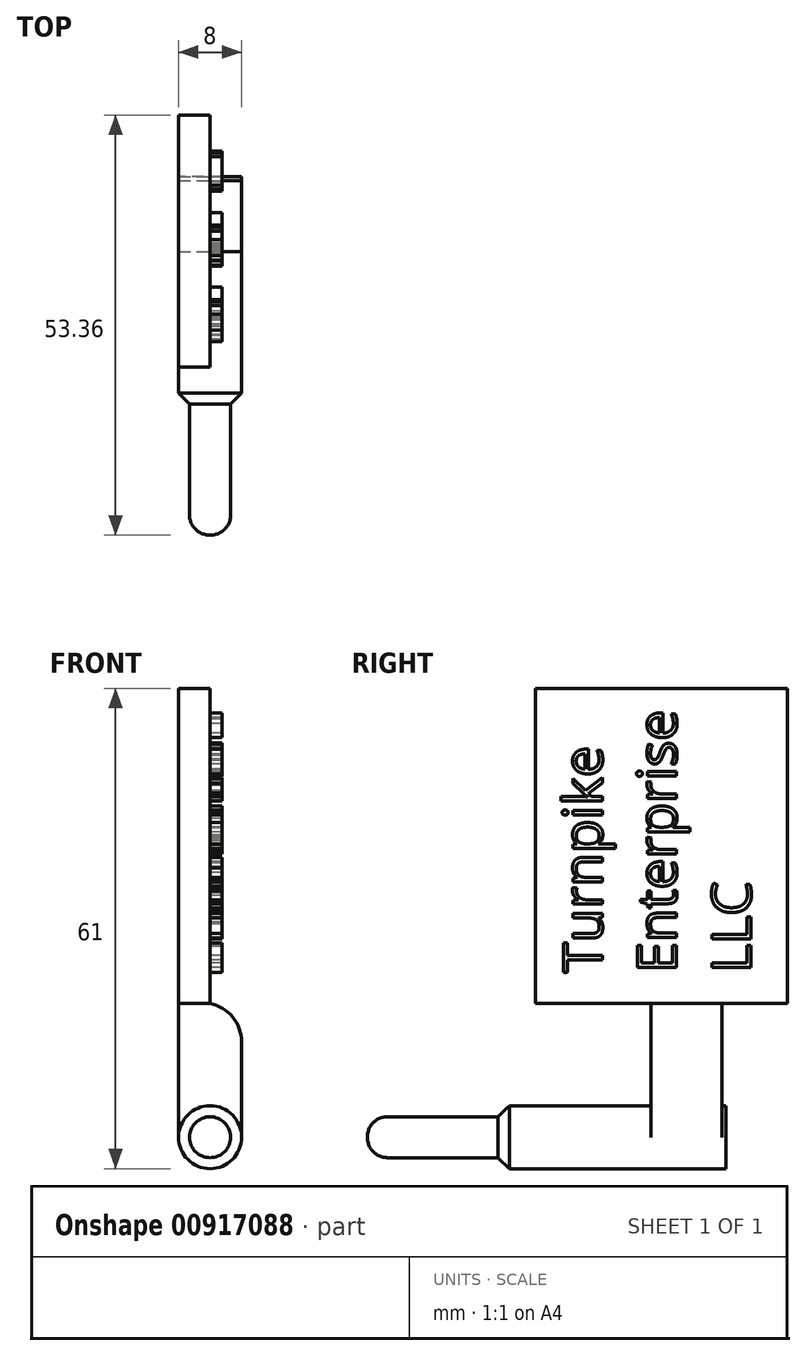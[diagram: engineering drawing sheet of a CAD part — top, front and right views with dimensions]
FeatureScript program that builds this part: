
annotation { "Feature Type Name" : "Feature", "Feature Type Description" : "" }
export const myFeature = defineFeature(function(context is Context, id is Id, definition is map)
    precondition{}
    {
        {
            var Q0;
            Q0=qCreatedBy(makeId("Right.planeOp"),FACE);
            var sketch = newSketch(context, id + "F0", { "sketchPlane" : qUnion([Q0])});
            skLineSegment(sketch, "E0.bottom", {"start": v(9, 0) * mm, "end": v(0, 0) * mm});
            skLineSegment(sketch, "E0.top", {"start": v(9, 17) * mm, "end": v(0, 17) * mm});
            skLineSegment(sketch, "E0.left", {"start": v(9, 0) * mm, "end": v(9, 17) * mm});
            skLineSegment(sketch, "E0.right", {"start": v(0, 0) * mm, "end": v(0, 17) * mm});
            skLineSegment(sketch, "E1.bottom", {"start": v(17.36, 17) * mm, "end": v(-14.64, 17) * mm});
            skLineSegment(sketch, "E1.top", {"start": v(17.36, 57) * mm, "end": v(-14.64, 57) * mm});
            skLineSegment(sketch, "E1.left", {"start": v(17.36, 17) * mm, "end": v(17.36, 57) * mm});
            skLineSegment(sketch, "E1.right", {"start": v(-14.64, 17) * mm, "end": v(-14.64, 57) * mm});
            skSolve(sketch);
        }
        {
            var Q0;
            Q0=qSketchRegion(id+"F0",true);
            extrude(context, id + "F1", {"entities" : qUnion([Q0]), "oppositeDirection" : true, "depth" : 4 * mm, "offsetDistance" : 25 * mm});
        }
        {
            var Q0;
            Q0=qCreatedBy(makeId("Front.planeOp"),FACE);
            var sketch = newSketch(context, id + "F2", { "sketchPlane" : qUnion([Q0])});
            skCircle(sketch, "E2", {"center": v(0, 0) * mm, "radius": 2.6 * mm});
            skSolve(sketch);
        }
        {
            var Q0;
            Q0=qSketchRegion(id+"F2",true);
            extrude(context, id + "F3", {"entities" : qUnion([Q0]), "operationType" : NewBodyOperationType.ADD, "depth" : 36 * mm, "offsetDistance" : 25 * mm});
        }
        {
            var Q0;
            Q0=qCreatedBy(makeId("Front.planeOp"),FACE);
            var sketch = newSketch(context, id + "F4", { "sketchPlane" : qUnion([Q0])});
            skCircle(sketch, "E3", {"center": v(0, 0) * mm, "radius": 4 * mm});
            skSolve(sketch);
        }
        {
            var Q0;
            Q0=qSketchRegion(id+"F4",true);
            extrude(context, id + "F5", {"entities" : qUnion([Q0]), "operationType" : NewBodyOperationType.ADD, "endBound" : BoundingType.SYMMETRIC, "depth" : 19 * mm, "offsetDistance" : 25 * mm});
        }
        {
            var Q0;
            Q0=qCreatedBy(makeId("Front.planeOp"),FACE);
            var sketch = newSketch(context, id + "F6", { "sketchPlane" : qUnion([Q0])});
            skCircle(sketch, "E4", {"center": v(0, 0) * mm, "radius": 4 * mm});
            skSolve(sketch);
        }
        {
            var Q0;
            Q0=qSketchRegion(id+"F6",true);
            extrude(context, id + "F7", {"entities" : qUnion([Q0]), "operationType" : NewBodyOperationType.ADD, "depth" : 20 * mm, "offsetDistance" : 25 * mm});
        }
        {
            var Q0;
            Q0=qCreatedBy(makeId("Right.planeOp"),FACE);
            var sketch = newSketch(context, id + "F8", { "sketchPlane" : qUnion([Q0])});
            skText(sketch, "E5", { "text": "Turnpike\nEnterprise\nLLC\n", "fontName": "OpenSans-Regular.ttf"});
            const initialGuessF8  = {"E5": [-0.00618, 0.0209, 0, 1, 0.005]};
            skSetInitialGuess(sketch, initialGuessF8);
            skSolve(sketch);
        }
        {
            var Q0;
            Q0=qSketchRegion(id+"F8",true);
            extrude(context, id + "F9", {"entities" : qUnion([Q0]), "operationType" : NewBodyOperationType.ADD, "depth" : 1.5 * mm, "offsetDistance" : 25 * mm});
        }
        {
            var Q0;
            Q0=makeQuery(id+"F7.opExtrude","CAP_EDGE",EDGE,{"disambiguationData":[OSD([sQuery(id+"F6.wireOp",EDGE,"E4")])],"isStart":false});
            chamfer(context, id + "F10", {"entities" : qUnion([Q0]), "width" : 2 * mm, "tangentPropagation" : true});
        }
        {
            var Q0;
            Q0=makeQuery(id+"F3.opExtrude","CAP_EDGE",EDGE,{"disambiguationData":[OSD([sQuery(id+"F2.wireOp",EDGE,"E2")])],"isStart":false});
            fillet(context, id + "F11", {"entities" : qUnion([Q0]), "radius" : 2.5 * mm, "tangentPropagation" : true, "allowEdgeOverflow" : false});
        }
        {
            var Q0;
            Q0=qCreatedBy(makeId("Front.planeOp"),FACE);
            var sketch = newSketch(context, id + "F12", { "sketchPlane" : qUnion([Q0])});
            skLineSegment(sketch, "E6.bottom", {"start": v(0, 17) * mm, "end": v(4, 17) * mm});
            skLineSegment(sketch, "E6.top", {"start": v(0, 0) * mm, "end": v(4, 0) * mm});
            skLineSegment(sketch, "E6.left", {"start": v(0, 17) * mm, "end": v(0, 0) * mm});
            skLineSegment(sketch, "E6.right", {"start": v(4, 17) * mm, "end": v(4, 0) * mm});
            skSolve(sketch);
        }
        {
            var Q0;
            Q0 = qSketchRegion(id + "F12", true);
            extrude(context, id + "F13", {"entities" : qUnion([Q0]), "operationType" : NewBodyOperationType.ADD, "oppositeDirection" : true, "depth" : 9 * mm, "offsetDistance" : 25 * mm});
        }
        {
            var Q0;
            Q0=makeQuery(id+"F13.opExtrude","SWEPT_EDGE",EDGE,{"disambiguationData":[OSD([sQuery(id+"F12.wireOp",EDGE,"E6.bottom"),sQuery(id+"F12.wireOp",EDGE,"E6.right")])]});
            fillet(context, id + "F14", {"entities" : qUnion([Q0]), "radius" : 5 * mm, "tangentPropagation" : true, "allowEdgeOverflow" : false});
        }
    });
